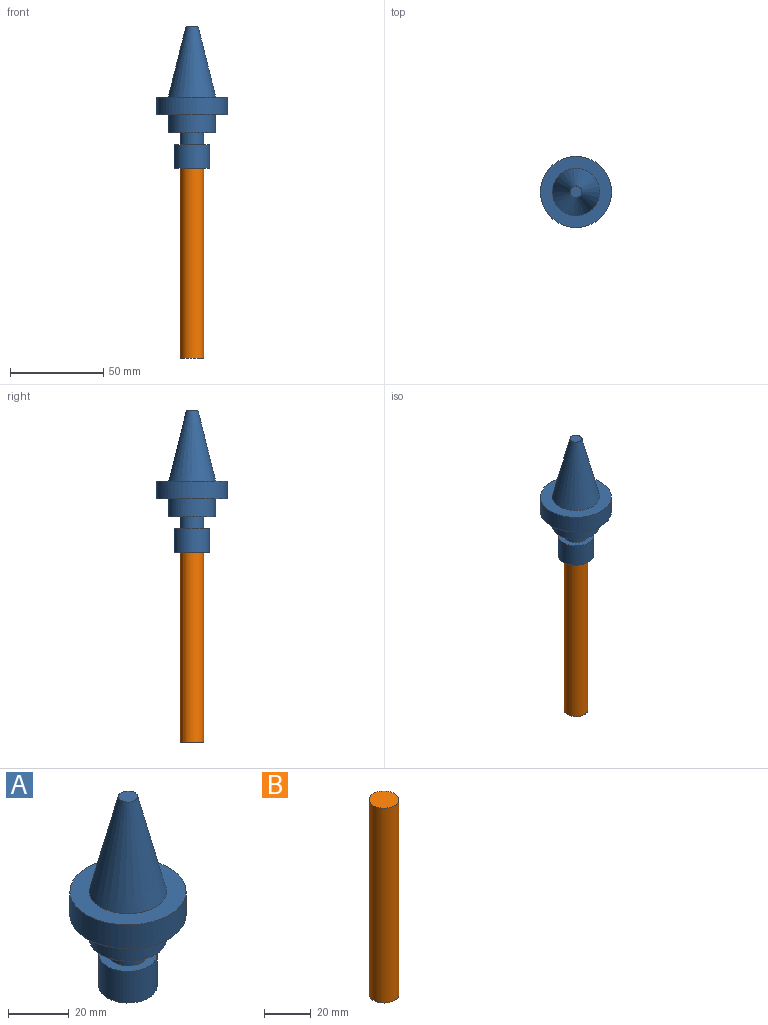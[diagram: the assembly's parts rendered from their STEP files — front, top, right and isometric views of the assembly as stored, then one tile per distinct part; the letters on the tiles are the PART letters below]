
ASSEMBLY  parts=2 mates=1
PART A: 11 faces, bbox 38.1x38.1x76.2 mm
  f0: plane 6.35x6.35mm, normal (0,0,1), area 31.7mm2, adj f1
  f1: cone r=3.17mm half-angle=14deg, axis (0,0,-1), area 1958.6mm2, adj f0,f2
  f2: plane 38.1x38.1mm, normal (0,0,1), area 633.4mm2, adj f1,f3
  f3: cylinder r=19.05mm len=38.1mm, axis (0,0,-1), area 1140.1mm2, adj f2,f4
  f4: plane 38.1x38.1mm, normal (0,0,-1), area 633.4mm2, adj f3,f5
  f5: cylinder r=12.7mm len=25.4mm, axis (0,0,-1), area 760.1mm2, adj f4,f6
  f6: plane 25.4x25.4mm, normal (0,0,-1), area 380mm2, adj f5,f7
  f7: cylinder r=6.35mm len=12.7mm, axis (0,0,-1), area 253.4mm2, adj f6,f8
  f8: plane 19.05x19.05mm, normal (0,0,1), area 158.3mm2, adj f7,f9
  f9: cylinder r=9.53mm len=19.05mm, axis (0,0,-1), area 760.1mm2, adj f8,f10
  f10: plane 19.05x19.05mm, normal (0,0,-1), area 285mm2, adj f9
PART B: 3 faces, bbox 12.7x12.7x101.6 mm
  f0: cylinder r=6.35mm len=101.6mm, axis (0,0,-1), area 4053.7mm2, adj f1,f2
  f1: plane 12.7x12.7mm, normal (0,0,1), area 126.7mm2, adj f0
  f2: plane 12.7x12.7mm, normal (0,0,-1), area 126.7mm2, adj f0
PLACE A at identity
PLACE B t=(0,0,-139.7)mm
MATE fastened B.f0 <-> A.f1  axis (0,0,1) through (0,0,-38.1)mm
